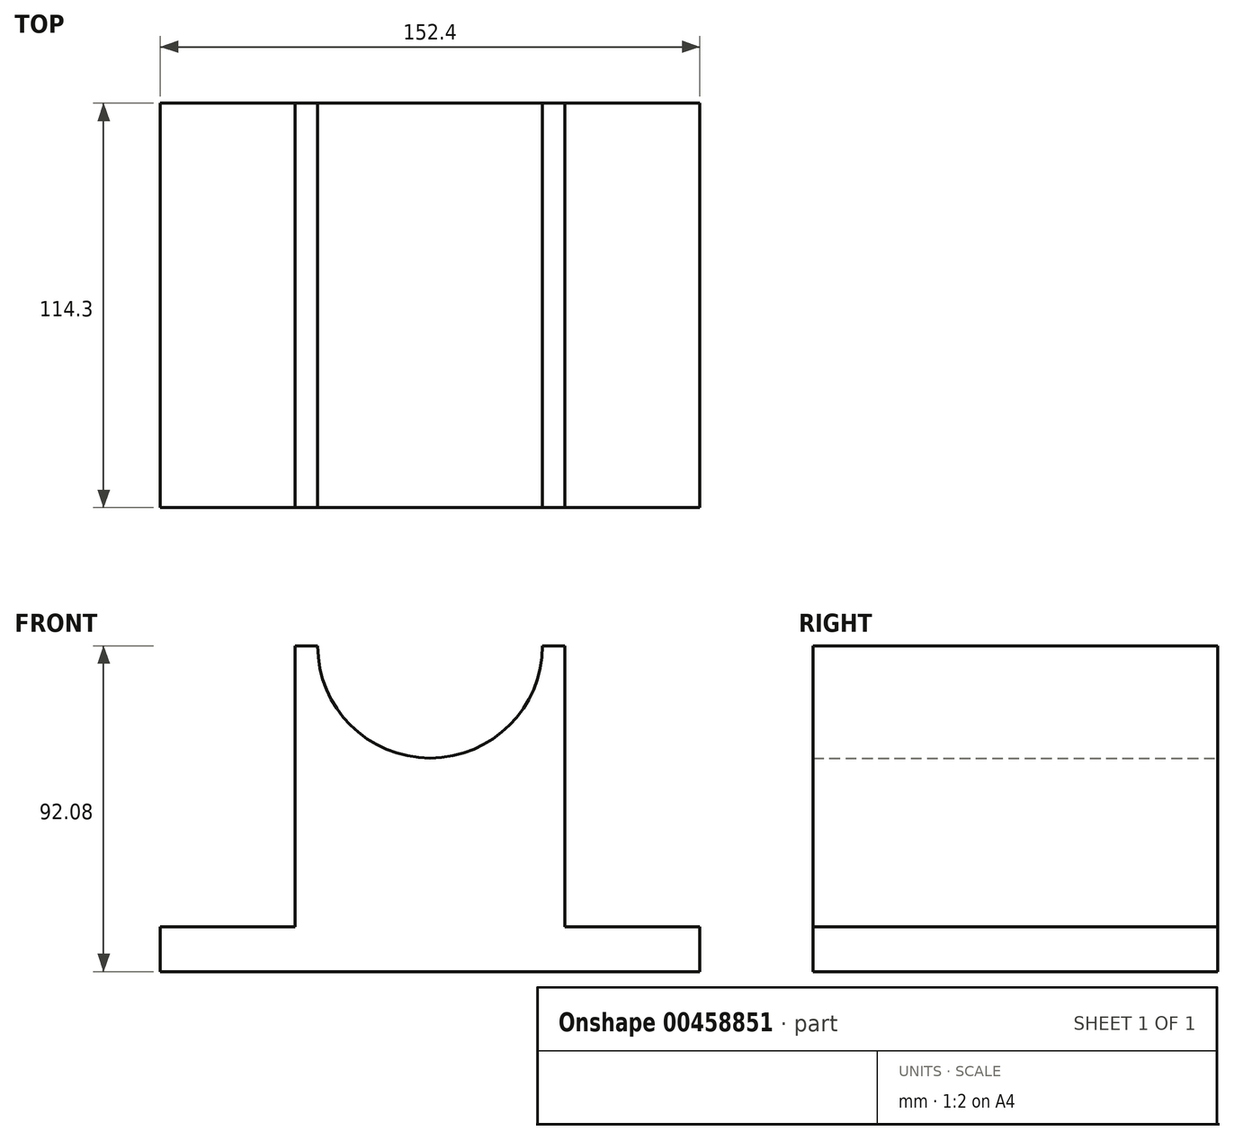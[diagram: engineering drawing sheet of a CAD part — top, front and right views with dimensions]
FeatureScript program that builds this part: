
annotation { "Feature Type Name" : "Feature", "Feature Type Description" : "" }
export const myFeature = defineFeature(function(context is Context, id is Id, definition is map)
    precondition{}
    {
        {
            var Q0;
            Q0=qCreatedBy(makeId("Front.planeOp"),FACE);
            var sketch = newSketch(context, id + "F0", { "sketchPlane" : qUnion([Q0])});
            skLineSegment(sketch, "E0", {"start": v(-97.58, -65.85) * mm, "end": v(-21.38, -65.85) * mm});
            skLineSegment(sketch, "E1", {"start": v(-97.58, -65.85) * mm, "end": v(-97.58, -53.15) * mm});
            skLineSegment(sketch, "E2", {"start": v(-97.58, -53.15) * mm, "end": v(-59.48, -53.15) * mm});
            skLineSegment(sketch, "E3", {"start": v(-59.48, -53.15) * mm, "end": v(-59.48, 26.23) * mm});
            skLineSegment(sketch, "E4", {"start": v(-59.48, 26.23) * mm, "end": v(-53.13, 26.23) * mm});
            skLineSegment(sketch, "E5.MirrorCS", {"start": v(16.72, 26.23) * mm, "end": v(10.37, 26.23) * mm});
            skLineSegment(sketch, "E6.MirrorCS", {"start": v(16.72, -53.15) * mm, "end": v(16.72, 26.23) * mm});
            skLineSegment(sketch, "E7.MirrorCS", {"start": v(54.82, -53.15) * mm, "end": v(16.72, -53.15) * mm});
            skLineSegment(sketch, "E8.MirrorCS", {"start": v(54.82, -65.85) * mm, "end": v(54.82, -53.15) * mm});
            skLineSegment(sketch, "E9.MirrorCS", {"start": v(54.82, -65.85) * mm, "end": v(-21.38, -65.85) * mm});
            skArc(sketch, "E10", {"start": v(10.37, 26.23) * mm, "mid": v(-21.38, -5.52) * mm, "end": v(-53.13, 26.23) * mm});
            skSolve(sketch);
        }
        {
            var Q0;
            Q0 = qSketchRegion(id + "F0", true);
            extrude(context, id + "F1", {"entities" : qUnion([Q0]), "depth" : 114.3 * mm});
        }
    });
